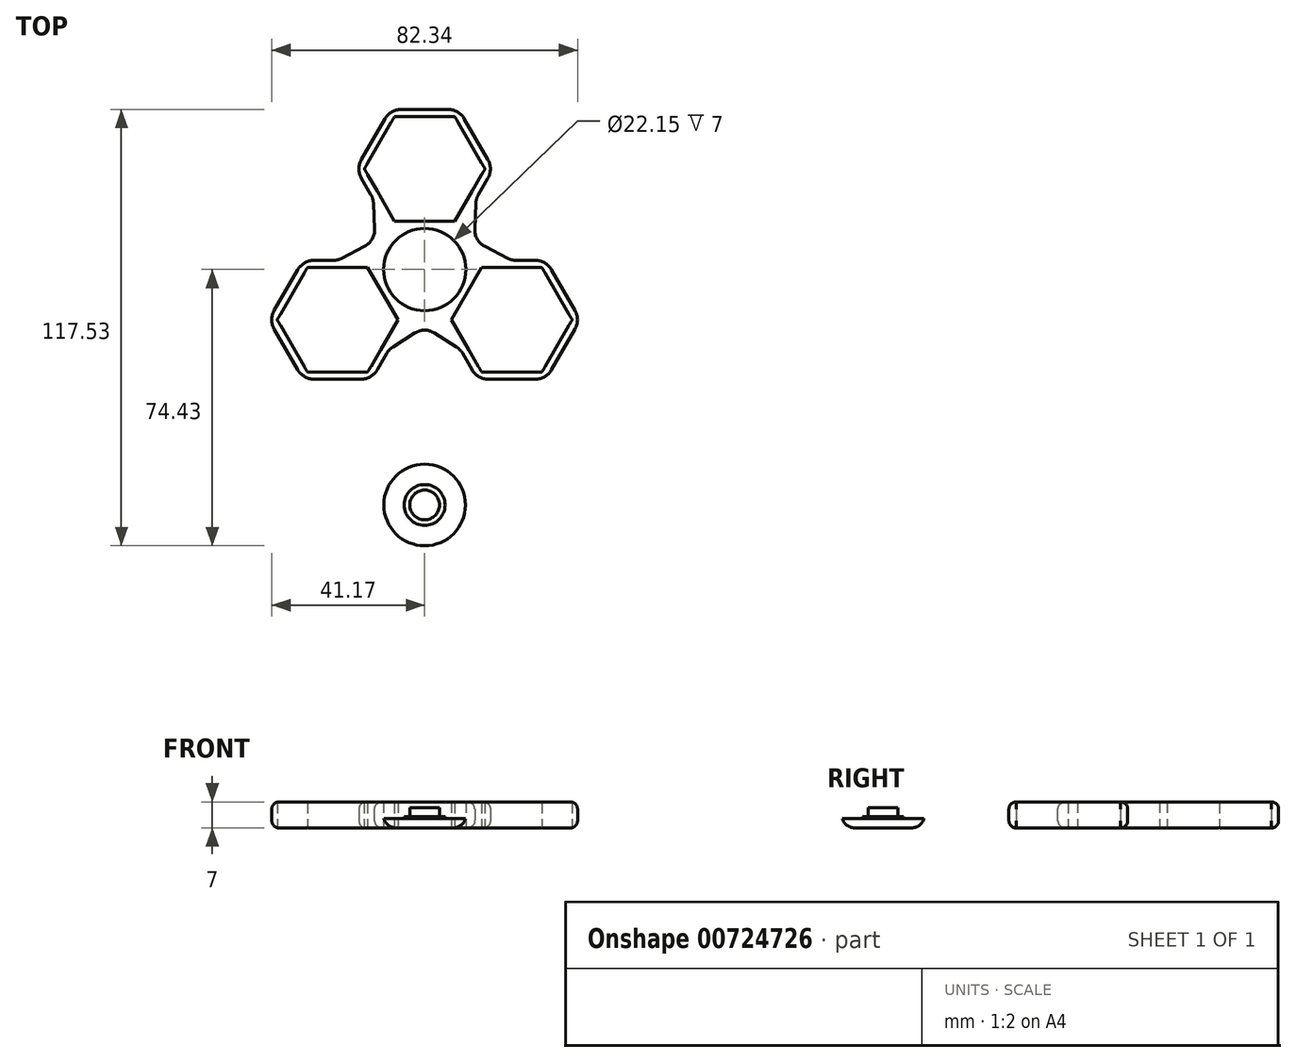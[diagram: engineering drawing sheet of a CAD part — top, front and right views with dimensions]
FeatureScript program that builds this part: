
annotation { "Feature Type Name" : "Feature", "Feature Type Description" : "" }
export const myFeature = defineFeature(function(context is Context, id is Id, definition is map)
    precondition{}
    {
        {
            var Q0;
            Q0=qCreatedBy(makeId("Top.planeOp"),FACE);
            var sketch = newSketch(context, id + "F0", { "sketchPlane" : qUnion([Q0])});
            skLineSegment(sketch, "E0", {"start": v(0, 0) * mm, "end": v(0, 27.1) * mm, "construction": true});
            skCircle(sketch, "E1", {"center": v(0, 0) * mm, "radius": 11.07 * mm});
            skCircle(sketch, "E2.cCircle", {"center": v(0, 27.1) * mm, "radius": 14.07 * mm, "construction": true});
            skLineSegment(sketch, "E2.0", {"start": v(8.13, 13.03) * mm, "end": v(-8.13, 13.03) * mm});
            skLineSegment(sketch, "E2.1", {"start": v(-8.13, 13.03) * mm, "end": v(-16.25, 27.1) * mm});
            skLineSegment(sketch, "E2.2", {"start": v(-16.25, 27.1) * mm, "end": v(-8.13, 41.18) * mm});
            skLineSegment(sketch, "E2.3", {"start": v(-8.13, 41.18) * mm, "end": v(8.13, 41.18) * mm});
            skLineSegment(sketch, "E2.4", {"start": v(8.13, 41.18) * mm, "end": v(16.25, 27.1) * mm});
            skLineSegment(sketch, "E2.5", {"start": v(16.25, 27.1) * mm, "end": v(8.13, 13.03) * mm});
            skPoint(sketch, "E2.0.midPoint", {"position": v(0, 13.03) * mm});
            skLineSegment(sketch, "E3.0", {"start": v(-18.48, 27.1) * mm, "end": v(-9.24, 43.1) * mm});
            skLineSegment(sketch, "E3.1", {"start": v(9.24, 43.1) * mm, "end": v(18.48, 27.1) * mm});
            skLineSegment(sketch, "E3.2", {"start": v(18.48, 27.1) * mm, "end": v(9.24, 11.1) * mm});
            skLineSegment(sketch, "E3.3", {"start": v(-9.24, 43.1) * mm, "end": v(9.24, 43.1) * mm});
            skLineSegment(sketch, "E3.4", {"start": v(9.24, 11.1) * mm, "end": v(-9.24, 11.1) * mm});
            skLineSegment(sketch, "E3.5", {"start": v(-9.24, 11.1) * mm, "end": v(-18.48, 27.1) * mm});
            skCircle(sketch, "E4.0", {"center": v(0, 0) * mm, "radius": 13 * mm});
            skLineSegment(sketch, "E5.top", {"start": v(11.11, 36) * mm, "end": v(10.9, 36) * mm});
            skLineSegment(sketch, "E6.trimOffspring", {"start": v(-10.9, 36) * mm, "end": v(-11.11, 36) * mm});
            skPoint(sketch, "E7.orphan", {"position": v(13.04, 36) * mm});
            skPoint(sketch, "E8.orphan", {"position": v(-15.46, 36) * mm});
            skLineSegment(sketch, "E9", {"start": v(13.86, 19.1) * mm, "end": v(13.01, 0) * mm});
            skLineSegment(sketch, "E10", {"start": v(-13, 0) * mm, "end": v(-13.86, 19.1) * mm});
            skLineSegment(sketch, "E11", {"start": v(-13, 0) * mm, "end": v(13.01, 0) * mm});
            skSolve(sketch);
        }
        {
            var Q0;
            Q0 = qSketchRegion(id + "F0", true);
            var Q1;
            {var subQ0=sQuery(id+"F0.wireOp",EDGE,"E4.0");var subQ1=sQuery(id+"F0.wireOp",EDGE,"E3.4");var subQ2=makeQuery(id+"F0.imprint","INTERSECT",VERTEX,{"disambiguationData":[OD(0.0)],"derivedFrom":[subQ1,subQ0]});Q1=makeQuery(id+"F0.imprint","IMPRINT",FACE,{"disambiguationData":[TD([[makeQuery(id+"F0.imprint","IMPRINT",EDGE,{"disambiguationData":[TD([[subQ2,-1.0]])],"derivedFrom":subQ1}),-1.0]])]});}
            extrude(context, id + "F1", {"entities" : qUnion([Q0, Q1]), "depth" : 7 * mm, "offsetDistance" : 25 * mm});
        }
        {
            var Q0;
            Q0=makeQuery(id+"F1.opExtrude","SWEPT_EDGE",EDGE,{"disambiguationData":[OSD([sQuery(id+"F0.wireOp",EDGE,"E3.0"),sQuery(id+"F0.wireOp",EDGE,"E3.5")])]});
            var Q1;
            Q1=makeQuery(id+"F1.opExtrude","SWEPT_EDGE",EDGE,{"disambiguationData":[OSD([sQuery(id+"F0.wireOp",EDGE,"E3.0"),sQuery(id+"F0.wireOp",EDGE,"E3.3")])]});
            var Q2;
            Q2=makeQuery(id+"F1.opExtrude","SWEPT_EDGE",EDGE,{"disambiguationData":[OSD([sQuery(id+"F0.wireOp",EDGE,"E3.1"),sQuery(id+"F0.wireOp",EDGE,"E3.3")])]});
            var Q3;
            Q3=makeQuery(id+"F1.opExtrude","SWEPT_EDGE",EDGE,{"disambiguationData":[OSD([sQuery(id+"F0.wireOp",EDGE,"E3.1"),sQuery(id+"F0.wireOp",EDGE,"E3.2")])]});
            var Q4;
            Q4=makeQuery(id+"F1.opExtrude","SWEPT_EDGE",EDGE,{"disambiguationData":[OSD([sQuery(id+"F0.wireOp",EDGE,"E3.2"),sQuery(id+"F0.wireOp",EDGE,"E5.left")])]});
            var Q5;
            Q5=makeQuery(id+"F1.opExtrude","SWEPT_EDGE",EDGE,{"disambiguationData":[OSD([sQuery(id+"F0.wireOp",EDGE,"E3.5"),sQuery(id+"F0.wireOp",EDGE,"E5.right")])]});
            fillet(context, id + "F2", {"entities" : qUnion([Q0, Q1, Q2, Q3, Q4, Q5]), "radius" : 5 * mm, "tangentPropagation" : true, "allowEdgeOverflow" : false});
        }
        {
            var Q0;
            Q0=makeQuery(id+"F1.opExtrude","SWEPT_BODY",BODY,{"disambiguationData":[OSD([sQuery(id+"F0.wireOp",EDGE,"E1"),sQuery(id+"F0.wireOp",EDGE,"E2.0"),sQuery(id+"F0.wireOp",EDGE,"E2.1"),sQuery(id+"F0.wireOp",EDGE,"E2.2"),sQuery(id+"F0.wireOp",EDGE,"E2.3"),sQuery(id+"F0.wireOp",EDGE,"E2.4"),sQuery(id+"F0.wireOp",EDGE,"E2.5"),sQuery(id+"F0.wireOp",EDGE,"E3.0"),sQuery(id+"F0.wireOp",EDGE,"E3.1"),sQuery(id+"F0.wireOp",EDGE,"E3.2"),sQuery(id+"F0.wireOp",EDGE,"E3.3"),sQuery(id+"F0.wireOp",EDGE,"E3.5"),sQuery(id+"F0.wireOp",EDGE,"E4.0"),sQuery(id+"F0.wireOp",EDGE,"E5.left"),sQuery(id+"F0.wireOp",EDGE,"E5.right")])]});
            var Q1;
            Q1=makeQuery(id+"F1.opExtrude","SWEPT_FACE",FACE,{"disambiguationData":[OSD([sQuery(id+"F0.wireOp",EDGE,"E1")])]});
            circularPattern(context, id + "F3", {"operationType" : NewBodyOperationType.ADD, "entities" : qUnion([Q0]), "axis" : qUnion([Q1]), "angle" : 360 * degree, "instanceCount" : 3, "equalSpace" : true});
        }
        {
            var Q0;
            Q0=makeQuery(id+"F3.boolean.opBoolean","INTERSECT",EDGE,{"derivedFrom":[makeQuery(id+"F1.opExtrude","SWEPT_FACE",FACE,{"disambiguationData":[OSD([sQuery(id+"F0.wireOp",EDGE,"E9")])]}),makeQuery(id+"F3.opPattern","COPY",FACE,{"derivedFrom":makeQuery(id+"F1.opExtrude","SWEPT_FACE",FACE,{"disambiguationData":[OSD([sQuery(id+"F0.wireOp",EDGE,"E10")])]}),"instanceName":"2"})]});
            var Q1;
            Q1=makeQuery(id+"F3.boolean.opBoolean","INTERSECT",EDGE,{"derivedFrom":[makeQuery(id+"F3.opPattern","COPY",FACE,{"derivedFrom":makeQuery(id+"F1.opExtrude","SWEPT_FACE",FACE,{"disambiguationData":[OSD([sQuery(id+"F0.wireOp",EDGE,"E10")])]}),"instanceName":"1"}),makeQuery(id+"F3.opPattern","COPY",FACE,{"derivedFrom":makeQuery(id+"F1.opExtrude","SWEPT_FACE",FACE,{"disambiguationData":[OSD([sQuery(id+"F0.wireOp",EDGE,"E9")])]}),"instanceName":"2"})]});
            var Q2;
            Q2=makeQuery(id+"F3.boolean.opBoolean","INTERSECT",EDGE,{"derivedFrom":[makeQuery(id+"F1.opExtrude","SWEPT_FACE",FACE,{"disambiguationData":[OSD([sQuery(id+"F0.wireOp",EDGE,"E10")])]}),makeQuery(id+"F3.opPattern","COPY",FACE,{"derivedFrom":makeQuery(id+"F1.opExtrude","SWEPT_FACE",FACE,{"disambiguationData":[OSD([sQuery(id+"F0.wireOp",EDGE,"E9")])]}),"instanceName":"1"})]});
            fillet(context, id + "F4", {"entities" : qUnion([Q0, Q1, Q2]), "radius" : 5 * mm, "tangentPropagation" : true, "allowEdgeOverflow" : false});
        }
        {
            var Q0;
            Q0=qCreatedBy(makeId("Top.planeOp"),FACE);
            var sketch = newSketch(context, id + "F5", { "sketchPlane" : qUnion([Q0])});
            skCircle(sketch, "E12", {"center": v(0, -63.43) * mm, "radius": 11 * mm});
            skCircle(sketch, "E13", {"center": v(0, -63.43) * mm, "radius": 4 * mm});
            skCircle(sketch, "E14", {"center": v(0, -63.43) * mm, "radius": 5.5 * mm});
            skSolve(sketch);
        }
        {
            var Q0;
            Q0=makeQuery(id+"F5.imprint","IMPRINT",FACE,{"disambiguationData":[TD([[makeQuery(id+"F5.imprint","IMPRINT",EDGE,{"derivedFrom":sQuery(id+"F5.wireOp",EDGE,"E12")}),1.0]])]});
            extrude(context, id + "F6", {"entities" : qUnion([Q0]), "depth" : 2.5 * mm, "offsetDistance" : 25 * mm});
        }
        {
            var Q0;
            Q0=makeQuery(id+"F5.imprint","IMPRINT",FACE,{"disambiguationData":[TD([[makeQuery(id+"F5.imprint","IMPRINT",EDGE,{"derivedFrom":sQuery(id+"F5.wireOp",EDGE,"E13")}),-1.0]])]});
            var Q1;
            Q1=makeQuery(id+"F6.opExtrude","CAP_FACE",FACE,{"disambiguationData":[OSD([sQuery(id+"F5.wireOp",EDGE,"E12"),sQuery(id+"F5.wireOp",EDGE,"E14")])],"isStart":false});
            extrude(context, id + "F7", {"entities" : qUnion([Q0]), "operationType" : NewBodyOperationType.ADD, "endBound" : BoundingType.UP_TO_SURFACE, "depth" : 25 * mm, "endBoundEntityFace" : qUnion([Q1]), "hasOffset" : true, "offsetDistance" : .5 * mm, "offsetOppositeDirection" : true});
        }
        {
            var Q0;
            Q0=makeQuery(id+"F5.imprint","IMPRINT",FACE,{"disambiguationData":[TD([[makeQuery(id+"F5.imprint","IMPRINT",EDGE,{"derivedFrom":sQuery(id+"F5.wireOp",EDGE,"E13")}),1.0]])]});
            var Q1;
            Q1=makeQuery(id+"F7.opExtrude","CAP_FACE",FACE,{"disambiguationData":[OSD([sQuery(id+"F5.wireOp",EDGE,"E12"),sQuery(id+"F5.wireOp",EDGE,"E14")])],"isStart":false});
            extrude(context, id + "F8", {"entities" : qUnion([Q0]), "operationType" : NewBodyOperationType.ADD, "endBound" : BoundingType.UP_TO_SURFACE, "depth" : 3 * mm, "endBoundEntityFace" : qUnion([Q1]), "hasOffset" : true, "offsetDistance" : 2.5 * mm, "offsetOppositeDirection" : true});
        }
        {
            var Q0;
            {var subQ0=sQuery(id+"F5.wireOp",EDGE,"E13");var subQ1=sQuery(id+"F5.wireOp",EDGE,"E14");Q0=makeQuery(id+"F8.boolean.opBoolean","MERGE",FACE,{"derivedFrom":[makeQuery(id+"F7.boolean.opBoolean","MERGE",FACE,{"derivedFrom":[makeQuery(id+"F6.opExtrude","CAP_FACE",FACE,{"disambiguationData":[OSD([sQuery(id+"F5.wireOp",EDGE,"E12"),subQ1])],"isStart":true}),makeQuery(id+"F7.opExtrude","CAP_FACE",FACE,{"disambiguationData":[OSD([subQ0,subQ1])],"isStart":true})]}),makeQuery(id+"F8.opExtrude","CAP_FACE",FACE,{"disambiguationData":[OSD([subQ0])],"isStart":true})]});}
            fillet(context, id + "F9", {"entities" : qUnion([Q0]), "radius" : 3.5 * mm, "tangentPropagation" : true, "allowEdgeOverflow" : false});
        }
        {
            var Q0;
            Q0=makeQuery(id+"F1.opExtrude","CAP_EDGE",EDGE,{"disambiguationData":[OSD([sQuery(id+"F0.wireOp",EDGE,"E9")])],"isStart":false});
            var Q1;
            Q1=makeQuery(id+"F1.opExtrude","CAP_EDGE",EDGE,{"disambiguationData":[OSD([sQuery(id+"F0.wireOp",EDGE,"E9")])],"isStart":true});
            fillet(context, id + "F10", {"entities" : qUnion([Q0, Q1]), "radius" : 1.93 * mm, "tangentPropagation" : true, "allowEdgeOverflow" : false});
        }
    });
